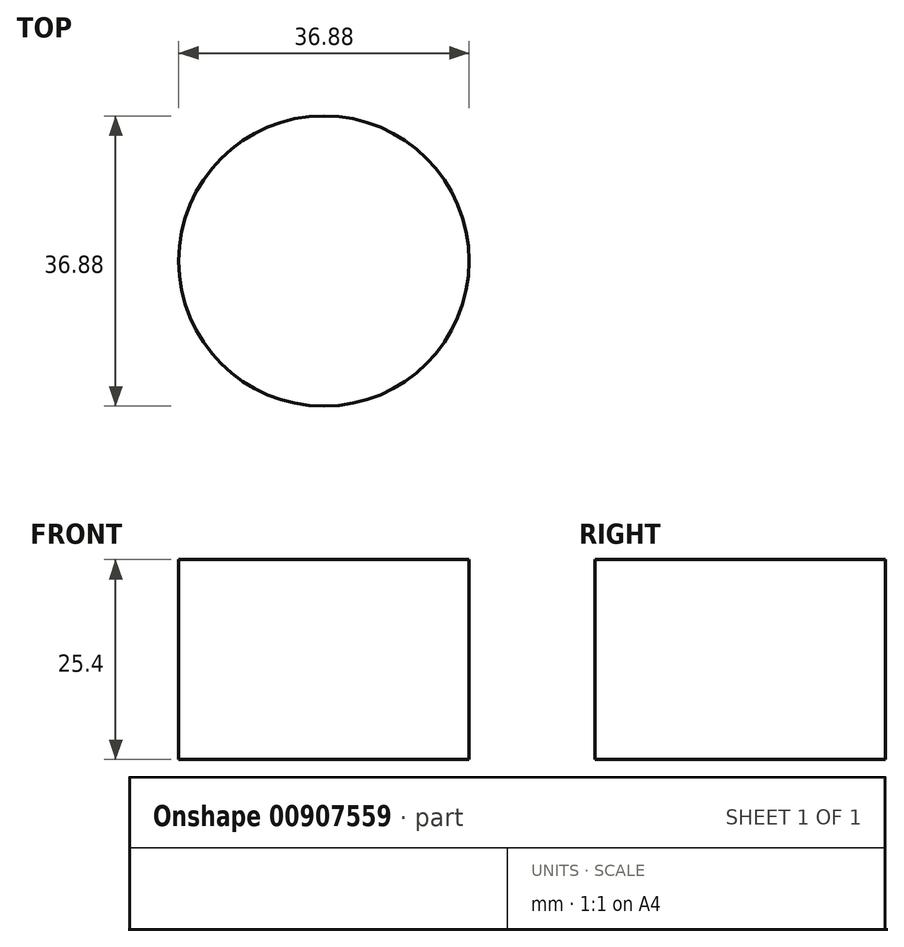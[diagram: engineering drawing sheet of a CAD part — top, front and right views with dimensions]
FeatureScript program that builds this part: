
annotation { "Feature Type Name" : "Feature", "Feature Type Description" : "" }
export const myFeature = defineFeature(function(context is Context, id is Id, definition is map)
    precondition{}
    {
        {
            var Q0;
            Q0=qCreatedBy(makeId("Top.planeOp"),FACE);
            var sketch = newSketch(context, id + "F0", { "sketchPlane" : qUnion([Q0])});
            skCircle(sketch, "E0", {"center": v(-53.46, 28.97) * mm, "radius": 18.44 * mm});
            skSolve(sketch);
        }
        {
            var Q0;
            Q0 = qSketchRegion(id + "F0", true);
            extrude(context, id + "F1", {"entities" : qUnion([Q0]), "depth" : 25.4 * mm, "offsetDistance" : 25.4 * mm});
        }
    });
